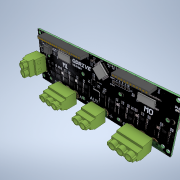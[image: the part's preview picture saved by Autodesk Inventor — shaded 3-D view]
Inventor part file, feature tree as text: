
AUTODESK INVENTOR PART (.ipt)
format: ipt  version: 2021.2 (Build 252289000, 289)  size: 3,479,552 bytes
history: native  units: mm
features: other x64, sketch x16, extrude x13, direct_edit x3, move_body x3, pattern_linear x2
ambient origin geometry x8: Origin, YZ Plane, XZ Plane, XY Plane, X Axis, Y Axis, Z Axis, Center Point
bodies: Solid1 (feature_tree)
feature tree (101):
  other  "PCB_Balance_PCB_v3.5 v3_TOP_Shrinkwrap_1.ipt"
  direct_edit  "Direct Edit1"
  direct_edit  "Direct Edit2"
  direct_edit  "Direct Edit3"
  extrude  "Выдавливание1"  Depth=10.0mm
  extrude  "Выдавливание2"  Depth=17.0mm TaperAngle=0.0deg
  pattern_linear  "Прямоуг.массив1"  Spacing1=-70.25mm  [1 undecoded]
  extrude  "Выдавливание3"  TaperAngle=0.0deg  [1 undecoded]
  pattern_linear  "Прямоуг.массив2"  Spacing1=31.0mm  [1 undecoded]
  extrude  "Выдавливание4"  Depth=51.0mm
  extrude  "Выдавливание5"  Depth=29.5mm
  extrude  "Выдавливание6"  Depth=2.5mm
  extrude  "Выдавливание7"  Depth=18.3mm
  sketch  "Эскиз8"
  extrude  "Выдавливание8"  Depth=8.4mm TaperAngle=0.0deg
  extrude  "Выдавливание9"  Depth=1.0mm
  extrude  "Выдавливание10"  Depth=0.6mm
  sketch  "Эскиз10"
  extrude  "Выдавливание11"  Depth=0.6mm
  extrude  "Выдавливание12"  Depth=1.3mm
  extrude  "Выдавливание13"  TaperAngle=0.0deg  [1 undecoded]
  sketch  "Эскиз12"
  other  "С М1"
  other  "А М1"
  other  "- DC M0"
  other  "+ DC М0"
  other  "С М0"
  other  "А М0"
  sketch  "Эскиз13"
  other  "- DC M1"
  other  "+ DC M1"
  sketch  "Эскиз14"
  other  "J4 GND M0"
  other  "J4 Z M0"
  other  "J4 B M0"
  other  "J4 A M0"
  other  "J4 5 M0"
  other  "J4 3.3V M0"
  other  "J4 GND M1"
  other  "J4 Z M1"
  other  "J4 B M1"
  other  "J4 A M1"
  other  "J4 5V M1"
  other  "J4 3.3V M1"
  other  "J3 CND 1"
  other  "J3 CND 2"
  other  "J3 GPIO 8"
  other  "J3 GPOI 7"
  other  "J3 GPOI 6"
  other  "J3 GPOI 5"
  other  "J3 GPOI 4"
  other  "J3 GPOI 3"
  other  "J3 GPOI 2"
  other  "J3 GPOI 1"
  other  "J3 MOS1"
  other  "J3 MOS0"
  other  "J3 SCK"
  other  "J3 AGND"
  other  "J3 AVCC"
  other  "J3 GND 3"
  other  "J3 CAN L"
  other  "J3 CAN H"
  other  "J3 GND 4"
  other  "J3 3.3V"
  other  "Маркировка1"
  other  "Маркировка2"
  other  "Solid1::PCB_Balance_PCB_v3.5 v3_TOP_Shrinkwrap_1.ipt"
  other  "Solid2::PCB_Balance_PCB_v3.5 v3_TOP_Shrinkwrap_1.ipt"
  other  "Solid3::PCB_Balance_PCB_v3.5 v3_TOP_Shrinkwrap_1.ipt"
  other  "Solid4::PCB_Balance_PCB_v3.5 v3_TOP_Shrinkwrap_1.ipt"
  other  "Solid5::PCB_Balance_PCB_v3.5 v3_TOP_Shrinkwrap_1.ipt"
  other  "Solid6::PCB_Balance_PCB_v3.5 v3_TOP_Shrinkwrap_1.ipt"
  other  "Solid7::PCB_Balance_PCB_v3.5 v3_TOP_Shrinkwrap_1.ipt"
  other  "Solid8::PCB_Balance_PCB_v3.5 v3_TOP_Shrinkwrap_1.ipt"
  other  "Solid9::PCB_Balance_PCB_v3.5 v3_TOP_Shrinkwrap_1.ipt"
  other  "Solid10::PCB_Balance_PCB_v3.5 v3_TOP_Shrinkwrap_1.ipt"
  other  "Solid11::PCB_Balance_PCB_v3.5 v3_TOP_Shrinkwrap_1.ipt"
  other  "Solid12::PCB_Balance_PCB_v3.5 v3_TOP_Shrinkwrap_1.ipt"
  other  "Solid13::PCB_Balance_PCB_v3.5 v3_TOP_Shrinkwrap_1.ipt"
  other  "Solid14::PCB_Balance_PCB_v3.5 v3_TOP_Shrinkwrap_1.ipt"
  other  "Solid15::PCB_Balance_PCB_v3.5 v3_TOP_Shrinkwrap_1.ipt"
  other  "Solid16::PCB_Balance_PCB_v3.5 v3_TOP_Shrinkwrap_1.ipt"
  other  "TaggingFeature1"
  sketch  "Эскиз1"
  other  "Твердое тело2"
  sketch  "Эскиз2"
  sketch  "Эскиз3"
  sketch  "Эскиз4"
  other  "Твердое тело3"
  sketch  "Эскиз5"
  sketch  "Эскиз6"
  sketch  "Эскиз7"
  sketch  "Эскиз9"
  sketch  "Эскиз11"
  sketch  "Эскиз15"
  other  "Картинка2"
  sketch  "Эскиз16"
  other  "Картинка3"
  move_body  "Move1"
  move_body  "Move2"
  move_body  "Move3"
note: 4 required parameter values undecoded (feature->parameter linkage not recoverable at this tier; creation-order binding heuristic only, values carry confidence <= 0.55)
